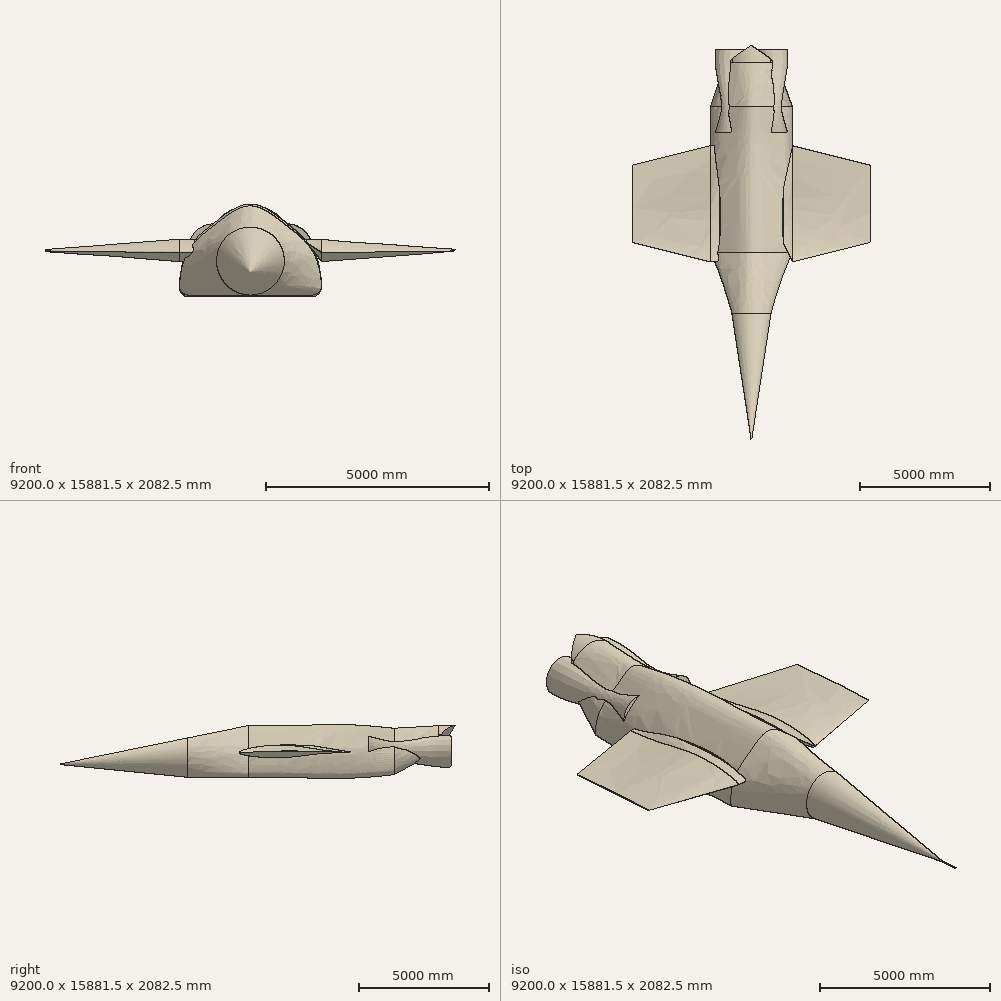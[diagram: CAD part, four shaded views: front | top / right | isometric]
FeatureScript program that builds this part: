
annotation { "Feature Type Name" : "Feature", "Feature Type Description" : "" }
export const myFeature = defineFeature(function(context is Context, id is Id, definition is map)
    precondition{}
    {
        {
            var Q0;
            Q0=qCreatedBy(makeId("Right.planeOp"),FACE);
            var sketch = newSketch(context, id + "F0", { "sketchPlane" : qUnion([Q0])});
            skLineSegment(sketch, "E0", {"start": v(0, 0) * mm, "end": v(-1750, 0) * mm});
            skLineSegment(sketch, "E1", {"start": v(-1750, 0) * mm, "end": v(-3500, 0) * mm});
            skLineSegment(sketch, "E2", {"start": v(-3500, 0) * mm, "end": v(-3500, -1000) * mm});
            skLineSegment(sketch, "E3", {"start": v(-3500, -1000) * mm, "end": v(-8500, -1000) * mm});
            skLineSegment(sketch, "E4", {"start": v(-8500, -1000) * mm, "end": v(-8500, -499.31) * mm});
            skLineSegment(sketch, "E5", {"start": v(-1151.4, 0) * mm, "end": v(-1151.4, 1000) * mm});
            skLineSegment(sketch, "E6", {"start": v(-1151.4, 1000) * mm, "end": v(-8500, -499.31) * mm});
            skLineSegment(sketch, "E7", {"start": v(-8500, -499.31) * mm, "end": v(-3500, -1000) * mm});
            skLineSegment(sketch, "E8", {"start": v(-3500, 0) * mm, "end": v(-3500, 520.82) * mm});
            skLineSegment(sketch, "E9", {"start": v(-8500, -499.31) * mm, "end": v(-8450, -499.31) * mm});
            skLineSegment(sketch, "E10", {"start": v(-8450, -499.31) * mm, "end": v(-8450, -489.1) * mm});
            skLineSegment(sketch, "E11", {"start": v(-8450, -499.31) * mm, "end": v(-8450, -504.32) * mm});
            skSolve(sketch);
        }
        {
            var Q0;
            Q0=sQuery(id+"F0.wireOp",EDGE,"E5");
            cPlane(context, id + "F1", {"entities" : qUnion([Q0]), "cplaneType" : CPlaneType.LINE_ANGLE, "offset" : 25 * mm, "angle" : 90 * degree, "oppositeDirection" : true, "width" : 150 * mm, "height" : 150 * mm});
        }
        {
            var Q0;
            Q0=qCreatedBy(id+"F1.planeOp",FACE);
            var sketch = newSketch(context, id + "F2", { "sketchPlane" : qUnion([Q0])});
            skLineSegment(sketch, "E12.top", {"start": v(-1394.2, -1000) * mm, "end": v(1394.2, -1000) * mm});
            skPoint(sketch, "E12.middle", {"position": v(0, 0) * mm});
            skFitSpline(sketch, "E13", {"points": [v(-1600, -1000) * mm, v(-848, 530) * mm, v(0, 1000) * mm, v(848, 530) * mm, v(1600, -1000) * mm], "startDerivative": vector(0, 10524.75) * mm, "endDerivative": vector(0, -10524.75) * mm});
            skArc(sketch, "E14", {"start": v(-735.27, 618.52) * mm, "mid": v(-1273.27, 435.52) * mm, "end": v(-1440.68, -107.53) * mm});
            skArc(sketch, "E15", {"start": v(1440.68, -107.53) * mm, "mid": v(1273.27, 435.52) * mm, "end": v(735.27, 618.52) * mm});
            skFitSpline(sketch, "E16.trimOffspring", {"points": [v(-1600, -1000) * mm, v(-848, 530) * mm, v(0, 1000) * mm, v(848, 530) * mm, v(1600, -1000) * mm], "startDerivative": vector(0, 10524.75) * mm, "endDerivative": vector(0, -10524.75) * mm});
            skFitSpline(sketch, "E17.trimOffspring", {"points": [v(-1600, -1000) * mm, v(-848, 530) * mm, v(0, 1000) * mm, v(848, 530) * mm, v(1600, -1000) * mm], "startDerivative": vector(0, 10524.75) * mm, "endDerivative": vector(0, -10524.75) * mm});
            skArc(sketch, "E18.filletArc", {"start": v(-1593.82, -787.83) * mm, "mid": v(-1539.85, -937.05) * mm, "end": v(-1394.2, -1000) * mm});
            skArc(sketch, "E19.filletArc", {"start": v(1394.2, -1000) * mm, "mid": v(1539.85, -937.05) * mm, "end": v(1593.82, -787.83) * mm});
            skSolve(sketch);
        }
        {
            var Q0;
            Q0=qCreatedBy(makeId("Front.planeOp"),FACE);
            var sketch = newSketch(context, id + "F3", { "sketchPlane" : qUnion([Q0])});
            skLineSegment(sketch, "E20.top", {"start": v(-1394.2, -1000) * mm, "end": v(1394.2, -1000) * mm});
            skPoint(sketch, "E20.middle", {"position": v(0, 0) * mm});
            skFitSpline(sketch, "E21", {"points": [v(-1600, -1000) * mm, v(-848, 530) * mm, v(0, 1000) * mm, v(848, 530) * mm, v(1600, -1000) * mm], "startDerivative": vector(0, 10524.75) * mm, "endDerivative": vector(0, -10524.75) * mm});
            skArc(sketch, "E22", {"start": v(-735.27, 618.52) * mm, "mid": v(-1273.27, 435.52) * mm, "end": v(-1440.68, -107.53) * mm});
            skArc(sketch, "E23", {"start": v(1440.68, -107.53) * mm, "mid": v(1273.27, 435.52) * mm, "end": v(735.27, 618.52) * mm});
            skFitSpline(sketch, "E24.trimOffspring", {"points": [v(-1600, -1000) * mm, v(-848, 530) * mm, v(0, 1000) * mm, v(848, 530) * mm, v(1600, -1000) * mm], "startDerivative": vector(0, 10524.75) * mm, "endDerivative": vector(0, -10524.75) * mm});
            skFitSpline(sketch, "E25.trimOffspring", {"points": [v(-1600, -1000) * mm, v(-848, 530) * mm, v(0, 1000) * mm, v(848, 530) * mm, v(1600, -1000) * mm], "startDerivative": vector(0, 10524.75) * mm, "endDerivative": vector(0, -10524.75) * mm});
            skArc(sketch, "E26.filletArc", {"start": v(-1593.82, -787.83) * mm, "mid": v(-1539.85, -937.05) * mm, "end": v(-1394.2, -1000) * mm});
            skArc(sketch, "E27.filletArc", {"start": v(1394.2, -1000) * mm, "mid": v(1539.85, -937.05) * mm, "end": v(1593.82, -787.83) * mm});
            skSolve(sketch);
        }
        {
            var Q0;
            Q0=qCreatedBy(makeId("Front.planeOp"),FACE);
            cPlane(context, id + "F4", {"entities" : qUnion([Q0]), "cplaneType" : CPlaneType.OFFSET, "offset" : 3500 * mm, "oppositeDirection" : true, "width" : 150 * mm, "height" : 150 * mm});
        }
        {
            var Q0;
            Q0=qCreatedBy(id+"F4.planeOp",FACE);
            var sketch = newSketch(context, id + "F5", { "sketchPlane" : qUnion([Q0])});
            skLineSegment(sketch, "E28.top", {"start": v(-1394.2, -1000) * mm, "end": v(1394.2, -1000) * mm});
            skPoint(sketch, "E28.middle", {"position": v(0, 0) * mm});
            skFitSpline(sketch, "E29", {"points": [v(-1600, -1000) * mm, v(-848, 530) * mm, v(0, 1000) * mm, v(848, 530) * mm, v(1600, -1000) * mm], "startDerivative": vector(0, 10524.75) * mm, "endDerivative": vector(0, -10524.75) * mm});
            skArc(sketch, "E30", {"start": v(-735.27, 618.52) * mm, "mid": v(-1273.27, 435.52) * mm, "end": v(-1440.68, -107.53) * mm});
            skArc(sketch, "E31", {"start": v(1440.68, -107.53) * mm, "mid": v(1273.27, 435.52) * mm, "end": v(735.27, 618.52) * mm});
            skFitSpline(sketch, "E32.trimOffspring", {"points": [v(-1600, -1000) * mm, v(-848, 530) * mm, v(0, 1000) * mm, v(848, 530) * mm, v(1600, -1000) * mm], "startDerivative": vector(0, 10524.75) * mm, "endDerivative": vector(0, -10524.75) * mm});
            skFitSpline(sketch, "E33.trimOffspring", {"points": [v(-1600, -1000) * mm, v(-848, 530) * mm, v(0, 1000) * mm, v(848, 530) * mm, v(1600, -1000) * mm], "startDerivative": vector(0, 10524.75) * mm, "endDerivative": vector(0, -10524.75) * mm});
            skArc(sketch, "E34.filletArc", {"start": v(-1593.82, -787.83) * mm, "mid": v(-1539.85, -937.05) * mm, "end": v(-1394.2, -1000) * mm});
            skArc(sketch, "E35.filletArc", {"start": v(1394.2, -1000) * mm, "mid": v(1539.85, -937.05) * mm, "end": v(1593.82, -787.83) * mm});
            skSolve(sketch);
        }
        {
            var Q0;
            Q0=qCreatedBy(makeId("Front.planeOp"),FACE);
            cPlane(context, id + "F6", {"entities" : qUnion([Q0]), "cplaneType" : CPlaneType.OFFSET, "offset" : 4500 * mm, "oppositeDirection" : true, "width" : 150 * mm, "height" : 150 * mm});
        }
        {
            var Q0;
            Q0=qCreatedBy(id+"F6.planeOp",FACE);
            var sketch = newSketch(context, id + "F7", { "sketchPlane" : qUnion([Q0])});
            skLineSegment(sketch, "E36.top", {"start": v(-1413.07, -900) * mm, "end": v(1413.07, -900) * mm});
            skPoint(sketch, "E36.middle", {"position": v(0, 0) * mm});
            skFitSpline(sketch, "E37", {"points": [v(-1600, -900) * mm, v(-784.42, 441.24) * mm, v(0, 900) * mm, v(784.42, 441.24) * mm, v(1600, -900) * mm], "startDerivative": vector(0, 9508.62) * mm, "endDerivative": vector(0, -9508.62) * mm});
            skArc(sketch, "E38", {"start": v(-719.25, 488.69) * mm, "mid": v(-1131.76, 394.84) * mm, "end": v(-1324.66, 18.33) * mm});
            skArc(sketch, "E39", {"start": v(1324.66, 18.33) * mm, "mid": v(1131.76, 394.84) * mm, "end": v(719.25, 488.69) * mm});
            skFitSpline(sketch, "E40.trimOffspring", {"points": [v(-1600, -900) * mm, v(-784.42, 441.24) * mm, v(0, 900) * mm, v(784.42, 441.24) * mm, v(1600, -900) * mm], "startDerivative": vector(0, 9508.62) * mm, "endDerivative": vector(0, -9508.62) * mm});
            skFitSpline(sketch, "E41.trimOffspring", {"points": [v(-1600, -900) * mm, v(-784.42, 441.24) * mm, v(0, 900) * mm, v(784.42, 441.24) * mm, v(1600, -900) * mm], "startDerivative": vector(0, 9508.62) * mm, "endDerivative": vector(0, -9508.62) * mm});
            skArc(sketch, "E42.filletArc", {"start": v(-1592.48, -705.43) * mm, "mid": v(-1545.4, -842.02) * mm, "end": v(-1413.07, -900) * mm});
            skArc(sketch, "E43.filletArc", {"start": v(1413.07, -900) * mm, "mid": v(1545.4, -842.02) * mm, "end": v(1592.48, -705.43) * mm});
            skLineSegment(sketch, "E44", {"start": v(-719.25, 488.69) * mm, "end": v(-1324.66, 18.33) * mm, "construction": true});
            skLineSegment(sketch, "E45", {"start": v(719.25, 488.69) * mm, "end": v(1324.66, 18.33) * mm, "construction": true});
            skSolve(sketch);
        }
        {
            var Q0;
            Q0=qCreatedBy(makeId("Front.planeOp"),FACE);
            cPlane(context, id + "F8", {"entities" : qUnion([Q0]), "cplaneType" : CPlaneType.OFFSET, "offset" : 6232.05 * mm, "oppositeDirection" : true, "width" : 150 * mm, "height" : 150 * mm});
        }
        {
            var Q0;
            Q0=qCreatedBy(id+"F8.planeOp",FACE);
            var sketch = newSketch(context, id + "F9", { "sketchPlane" : qUnion([Q0])});
            skArc(sketch, "E46", {"start": v(998.61, 52.63) * mm, "mid": v(0, 1000) * mm, "end": v(-998.61, 52.63) * mm});
            skLineSegment(sketch, "E47", {"start": v(0, 0) * mm, "end": v(-948.68, 0) * mm});
            skLineSegment(sketch, "E48", {"start": v(0, 0) * mm, "end": v(948.68, 0) * mm});
            skLineSegment(sketch, "E49", {"start": v(0, 1000) * mm, "end": v(0, 675) * mm, "construction": true});
            skLineSegment(sketch, "E50", {"start": v(0, 675) * mm, "end": v(-737.82, 675) * mm, "construction": true});
            skLineSegment(sketch, "E51", {"start": v(0, 675) * mm, "end": v(737.82, 675) * mm, "construction": true});
            skPoint(sketch, "E52.visualSharp", {"position": v(-1000, 0) * mm});
            skArc(sketch, "E52.filletArc", {"start": v(-998.61, 52.63) * mm, "mid": v(-984.96, 15.59) * mm, "end": v(-948.68, 0) * mm});
            skPoint(sketch, "E53.visualSharp", {"position": v(1000, 0) * mm});
            skArc(sketch, "E53.filletArc", {"start": v(948.68, 0) * mm, "mid": v(984.96, 15.59) * mm, "end": v(998.61, 52.63) * mm});
            skSolve(sketch);
        }
        {
            var Q0;
            Q0=makeQuery(id+"F2.imprint","IMPRINT",FACE,{"disambiguationData":[TD([[makeQuery(id+"F2.imprint","IMPRINT",EDGE,{"derivedFrom":sQuery(id+"F2.wireOp",EDGE,"E12.top")}),1.0]])]});
            var Q1;
            Q1=makeQuery(id+"F3.imprint","IMPRINT",FACE,{"disambiguationData":[TD([[makeQuery(id+"F3.imprint","IMPRINT",EDGE,{"derivedFrom":sQuery(id+"F3.wireOp",EDGE,"E20.top")}),1.0]])]});
            var Q2;
            Q2=makeQuery(id+"F5.imprint","IMPRINT",FACE,{"disambiguationData":[TD([[makeQuery(id+"F5.imprint","IMPRINT",EDGE,{"derivedFrom":sQuery(id+"F5.wireOp",EDGE,"E28.top")}),1.0]])]});
            var Q3;
            Q3=makeQuery(id+"F7.imprint","IMPRINT",FACE,{"disambiguationData":[TD([[makeQuery(id+"F7.imprint","IMPRINT",EDGE,{"derivedFrom":sQuery(id+"F7.wireOp",EDGE,"E36.top")}),1.0]])]});
            loft(context, id + "F10", {"sheetProfilesArray" : [{ "sheetProfileEntities" : qUnion([Q0]) }, { "sheetProfileEntities" : qUnion([Q1]) }, { "sheetProfileEntities" : qUnion([Q2]) }, { "sheetProfileEntities" : qUnion([Q3]) }]});
        }
        {
            var Q0;
            Q0=sQuery(id+"F7.wireOp",EDGE,"E44");
            var Q1;
            Q1=sQuery(id+"F9.wireOp",VERTEX,"E50.end");
            cPlane(context, id + "F11", {"entities" : qUnion([Q0, Q1]), "cplaneType" : CPlaneType.LINE_ANGLE, "offset" : 25 * mm, "angle" : 180 * degree, "width" : 150 * mm, "height" : 150 * mm});
        }
        {
            var Q0;
            Q0=qCreatedBy(id+"F11.planeOp",FACE);
            var sketch = newSketch(context, id + "F12", { "sketchPlane" : qUnion([Q0])});
            skLineSegment(sketch, "E54", {"start": v(-589.34, 4526.34) * mm, "end": v(-612.8, 6268.32) * mm});
            skLineSegment(sketch, "E55", {"start": v(-1354.08, 4472.19) * mm, "end": v(-612.8, 6268.32) * mm});
            skSolve(sketch);
        }
        {
            var Q0;
            Q0=sQuery(id+"F7.wireOp",EDGE,"E45");
            var Q1;
            Q1=sQuery(id+"F9.wireOp",VERTEX,"E51.end");
            cPlane(context, id + "F13", {"entities" : qUnion([Q0, Q1]), "cplaneType" : CPlaneType.LINE_ANGLE, "offset" : 25 * mm, "angle" : 0 * degree, "width" : 150 * mm, "height" : 150 * mm});
        }
        {
            var Q0;
            Q0=qCreatedBy(id+"F13.planeOp",FACE);
            var sketch = newSketch(context, id + "F14", { "sketchPlane" : qUnion([Q0])});
            skLineSegment(sketch, "E56", {"start": v(589.34, 4526.34) * mm, "end": v(612.8, 6268.32) * mm});
            skLineSegment(sketch, "E57", {"start": v(1354.08, 4472.19) * mm, "end": v(612.8, 6268.32) * mm});
            skSolve(sketch);
        }
        {
            var Q1;
            Q1=makeQuery(id+"F10.opLoft","CAP_FACE",FACE,{"disambiguationData":[OSD([makeQuery(id+"F7.imprint","IMPRINT",FACE,{"disambiguationData":[TD([[makeQuery(id+"F7.imprint","IMPRINT",EDGE,{"derivedFrom":sQuery(id+"F7.wireOp",EDGE,"E36.top")}),1.0]])]})])],"isStart":true});
            var Q2;
            Q2=makeQuery(id+"F9.imprint","IMPRINT",FACE,{"disambiguationData":[TD([[makeQuery(id+"F9.imprint","IMPRINT",EDGE,{"derivedFrom":sQuery(id+"F9.wireOp",EDGE,"E46")}),1.0]])]});
            var Q3;
            Q3=sQuery(id+"F12.wireOp",EDGE,"E54");
            var Q4;
            Q4=sQuery(id+"F14.wireOp",EDGE,"E56");
            loft(context, id + "F15", {"operationType" : NewBodyOperationType.ADD, "addGuides" : true, "sheetProfilesArray" : [{ "sheetProfileEntities" : qUnion([Q1]) }, { "sheetProfileEntities" : qUnion([Q2]) }], "guidesArray" : [{ "guideEntities" : qUnion([Q3]), "guideDerivativeType" : LoftGuideDerivativeType.DEFAULT, "guideDerivativeMagnitude" : 1 }, { "guideEntities" : qUnion([Q4]), "guideDerivativeType" : LoftGuideDerivativeType.DEFAULT, "guideDerivativeMagnitude" : 1 }]});
        }
        {
            var Q0;
            Q0=makeQuery(id+"F15.opLoft","CAP_FACE",FACE,{"disambiguationData":[OSD([makeQuery(id+"F9.imprint","IMPRINT",FACE,{"disambiguationData":[TD([[makeQuery(id+"F9.imprint","IMPRINT",EDGE,{"derivedFrom":sQuery(id+"F9.wireOp",EDGE,"E46")}),1.0]])]})])],"isStart":true});
            extrude(context, id + "F16", {"entities" : qUnion([Q0]), "operationType" : NewBodyOperationType.ADD, "depth" : 649.4 * mm, "offsetDistance" : 25 * mm});
        }
        {
            var Q0;
            Q0=qCreatedBy(makeId("Right.planeOp"),FACE);
            var sketch = newSketch(context, id + "F17", { "sketchPlane" : qUnion([Q0])});
            skLineSegment(sketch, "E58", {"start": v(0, 0) * mm, "end": v(4500, 0) * mm});
            skLineSegment(sketch, "E59", {"start": v(4500, 0) * mm, "end": v(6232.05, 0) * mm});
            skLineSegment(sketch, "E60", {"start": v(4500, 0) * mm, "end": v(4500, 1000) * mm});
            skLineSegment(sketch, "E61", {"start": v(4500, 1000) * mm, "end": v(6881.46, 1000) * mm});
            skLineSegment(sketch, "E62", {"start": v(6881.46, 1000) * mm, "end": v(6881.46, -1000) * mm});
            skLineSegment(sketch, "E63", {"start": v(6881.46, 1000) * mm, "end": v(6232.05, 0) * mm});
            skLineSegment(sketch, "E64", {"start": v(6232.05, 0) * mm, "end": v(5582.64, -1000) * mm});
            skLineSegment(sketch, "E65", {"start": v(5582.64, -1000) * mm, "end": v(6881.46, -1000) * mm});
            skSolve(sketch);
        }
        {
            var Q0;
            Q0=makeQuery(id+"F17.imprint","IMPRINT",FACE,{"disambiguationData":[TD([[makeQuery(id+"F17.imprint","IMPRINT",EDGE,{"derivedFrom":sQuery(id+"F17.wireOp",EDGE,"E62")}),-1.0]])]});
            var Q1;
            Q1=sQuery(id+"F17.wireOp",EDGE,"E61");
            revolve(context, id + "F18", {"operationType" : NewBodyOperationType.REMOVE, "entities" : qUnion([Q0]), "axis" : qUnion([Q1]), "revolveType" : RevolveType.SYMMETRIC, "oppositeDirection" : true, "angle" : 182 * degree});
        }
        {
            var Q0;
            Q0=qCreatedBy(id+"F1.planeOp",FACE);
            var sketch = newSketch(context, id + "F19", { "sketchPlane" : qUnion([Q0])});
            skLineSegment(sketch, "E66.top", {"start": v(-1394.2, -1000) * mm, "end": v(1394.2, -1000) * mm});
            skPoint(sketch, "E66.middle", {"position": v(0, 0) * mm});
            skFitSpline(sketch, "E67", {"points": [v(-1600, -1000) * mm, v(-848, 530) * mm, v(0, 1000) * mm, v(848, 530) * mm, v(1600, -1000) * mm], "startDerivative": vector(0, 10524.75) * mm, "endDerivative": vector(0, -10524.75) * mm});
            skArc(sketch, "E68.filletArc", {"start": v(-1593.82, -787.83) * mm, "mid": v(-1539.85, -937.05) * mm, "end": v(-1394.2, -1000) * mm});
            skArc(sketch, "E69.filletArc", {"start": v(1394.2, -1000) * mm, "mid": v(1539.85, -937.05) * mm, "end": v(1593.82, -787.83) * mm});
            skLineSegment(sketch, "E70", {"start": v(-1593.82, -787.83) * mm, "end": v(-1394.2, -1000) * mm, "construction": true});
            skLineSegment(sketch, "E71", {"start": v(1593.82, -787.83) * mm, "end": v(1394.2, -1000) * mm, "construction": true});
            skSolve(sketch);
        }
        {
            var Q0;
            Q0=qCreatedBy(makeId("Front.planeOp"),FACE);
            cPlane(context, id + "F20", {"entities" : qUnion([Q0]), "cplaneType" : CPlaneType.OFFSET, "offset" : 3500 * mm, "width" : 150 * mm, "height" : 150 * mm});
        }
        {
            var Q0;
            Q0=qCreatedBy(id+"F20.planeOp",FACE);
            var sketch = newSketch(context, id + "F21", { "sketchPlane" : qUnion([Q0])});
            skCircle(sketch, "E72", {"center": v(0, -239.59) * mm, "radius": 760.41 * mm});
            skLineSegment(sketch, "E73", {"start": v(0, -1000) * mm, "end": v(0, -800) * mm, "construction": true});
            skLineSegment(sketch, "E74", {"start": v(0, -800) * mm, "end": v(-513.97, -800) * mm, "construction": true});
            skLineSegment(sketch, "E75", {"start": v(0, -800) * mm, "end": v(513.97, -800) * mm, "construction": true});
            skSolve(sketch);
        }
        {
            var Q0;
            Q0=qCreatedBy(makeId("Front.planeOp"),FACE);
            cPlane(context, id + "F22", {"entities" : qUnion([Q0]), "cplaneType" : CPlaneType.OFFSET, "offset" : 8450 * mm, "width" : 150 * mm, "height" : 150 * mm});
        }
        {
            var Q0;
            Q0=qCreatedBy(id+"F22.planeOp",FACE);
            var sketch = newSketch(context, id + "F23", { "sketchPlane" : qUnion([Q0])});
            skCircle(sketch, "E76", {"center": v(0, -496.71) * mm, "radius": 7.6 * mm});
            skSolve(sketch);
        }
        {
            var Q0;
            Q0=sQuery(id+"F19.wireOp",EDGE,"E70");
            var Q1;
            Q1=sQuery(id+"F21.wireOp",VERTEX,"E74.end");
            cPlane(context, id + "F24", {"entities" : qUnion([Q0, Q1]), "cplaneType" : CPlaneType.LINE_ANGLE, "offset" : 25 * mm, "angle" : 0 * degree, "width" : 150 * mm, "height" : 150 * mm});
        }
        {
            var Q0;
            Q0=qCreatedBy(id+"F24.planeOp",FACE);
            var sketch = newSketch(context, id + "F25", { "sketchPlane" : qUnion([Q0])});
            skLineSegment(sketch, "E77", {"start": v(3032.27, -230.44) * mm, "end": v(558.11, 518.4) * mm});
            skLineSegment(sketch, "E78", {"start": v(3032.27, -230.44) * mm, "end": v(558.11, 227.09) * mm});
            skSolve(sketch);
        }
        {
            var Q0;
            Q0=sQuery(id+"F19.wireOp",EDGE,"E71");
            var Q1;
            Q1=sQuery(id+"F21.wireOp",VERTEX,"E75.end");
            cPlane(context, id + "F26", {"entities" : qUnion([Q0, Q1]), "cplaneType" : CPlaneType.LINE_ANGLE, "offset" : 25 * mm, "angle" : 180 * degree, "width" : 150 * mm, "height" : 150 * mm});
        }
        {
            var Q0;
            Q0=qCreatedBy(id+"F26.planeOp",FACE);
            var sketch = newSketch(context, id + "F27", { "sketchPlane" : qUnion([Q0])});
            skLineSegment(sketch, "E79", {"start": v(-3032.27, -230.44) * mm, "end": v(-558.11, 518.4) * mm});
            skLineSegment(sketch, "E80", {"start": v(-3032.27, -230.44) * mm, "end": v(-558.11, 227.09) * mm});
            skSolve(sketch);
        }
        {
            var Q1;
            Q1=makeQuery(id+"F19.imprint","IMPRINT",FACE,{"disambiguationData":[TD([[makeQuery(id+"F19.imprint","IMPRINT",EDGE,{"derivedFrom":sQuery(id+"F19.wireOp",EDGE,"E66.top")}),1.0]])]});
            var Q2;
            Q2=makeQuery(id+"F21.imprint","IMPRINT",FACE,{"disambiguationData":[TD([[makeQuery(id+"F21.imprint","IMPRINT",EDGE,{"derivedFrom":sQuery(id+"F21.wireOp",EDGE,"E72")}),1.0]])]});
            var Q3;
            Q3=sQuery(id+"F25.wireOp",EDGE,"E77");
            var Q4;
            Q4=sQuery(id+"F27.wireOp",EDGE,"E79");
            loft(context, id + "F28", {"operationType" : NewBodyOperationType.ADD, "addGuides" : true, "sheetProfilesArray" : [{ "sheetProfileEntities" : qUnion([Q1]) }, { "sheetProfileEntities" : qUnion([Q2]) }], "guidesArray" : [{ "guideEntities" : qUnion([Q3]), "guideDerivativeType" : LoftGuideDerivativeType.DEFAULT, "guideDerivativeMagnitude" : 1 }, { "guideEntities" : qUnion([Q4]), "guideDerivativeType" : LoftGuideDerivativeType.DEFAULT, "guideDerivativeMagnitude" : 1 }]});
        }
        {
            var Q1;
            Q1=makeQuery(id+"F28.opLoft","CAP_FACE",FACE,{"disambiguationData":[OSD([makeQuery(id+"F21.imprint","IMPRINT",FACE,{"disambiguationData":[TD([[makeQuery(id+"F21.imprint","IMPRINT",EDGE,{"derivedFrom":sQuery(id+"F21.wireOp",EDGE,"E72")}),1.0]])]})])],"isStart":true});
            var Q2;
            Q2=makeQuery(id+"F23.imprint","IMPRINT",FACE,{"disambiguationData":[TD([[makeQuery(id+"F23.imprint","IMPRINT",EDGE,{"derivedFrom":sQuery(id+"F23.wireOp",EDGE,"E76")}),1.0]])]});
            loft(context, id + "F29", {"operationType" : NewBodyOperationType.ADD, "sheetProfilesArray" : [{ "sheetProfileEntities" : qUnion([Q1]) }, { "sheetProfileEntities" : qUnion([Q2]) }]});
        }
        {
            var Q0;
            Q0=makeQuery(id+"F29.opLoft","CAP_FACE",FACE,{"disambiguationData":[OSD([makeQuery(id+"F23.imprint","IMPRINT",FACE,{"disambiguationData":[TD([[makeQuery(id+"F23.imprint","IMPRINT",EDGE,{"derivedFrom":sQuery(id+"F23.wireOp",EDGE,"E76")}),1.0]])]})])],"isStart":true});
            extrude(context, id + "F30", {"entities" : qUnion([Q0]), "operationType" : NewBodyOperationType.ADD, "depth" : 550 * mm, "offsetDistance" : 25 * mm});
        }
        {
            var Q0;
            Q0=qCreatedBy(makeId("Front.planeOp"),FACE);
            cPlane(context, id + "F31", {"entities" : qUnion([Q0]), "cplaneType" : CPlaneType.OFFSET, "offset" : 3500 * mm, "oppositeDirection" : true, "width" : 150 * mm, "height" : 150 * mm});
        }
        {
            var Q0;
            Q0=qCreatedBy(id+"F31.planeOp",FACE);
            var sketch = newSketch(context, id + "F32", { "sketchPlane" : qUnion([Q0])});
            skCircle(sketch, "E81", {"center": v(-800, 0) * mm, "radius": 600 * mm});
            skCircle(sketch, "E82", {"center": v(800, 0) * mm, "radius": 600 * mm});
            skSolve(sketch);
        }
        {
            var Q0;
            Q0=qCreatedBy(makeId("Front.planeOp"),FACE);
            cPlane(context, id + "F33", {"entities" : qUnion([Q0]), "cplaneType" : CPlaneType.OFFSET, "offset" : 4500 * mm, "oppositeDirection" : true, "width" : 150 * mm, "height" : 150 * mm});
        }
        {
            var Q0;
            Q0=qCreatedBy(id+"F33.planeOp",FACE);
            var sketch = newSketch(context, id + "F34", { "sketchPlane" : qUnion([Q0])});
            skCircle(sketch, "E83", {"center": v(-800, 0) * mm, "radius": 400 * mm});
            skCircle(sketch, "E84", {"center": v(800, 0) * mm, "radius": 400 * mm});
            skSolve(sketch);
        }
        {
            var Q0;
            Q0=qCreatedBy(makeId("Front.planeOp"),FACE);
            cPlane(context, id + "F35", {"entities" : qUnion([Q0]), "cplaneType" : CPlaneType.OFFSET, "offset" : 6232.05 * mm, "oppositeDirection" : true, "width" : 150 * mm, "height" : 150 * mm});
        }
        {
            var Q0;
            Q0=qCreatedBy(id+"F35.planeOp",FACE);
            var sketch = newSketch(context, id + "F36", { "sketchPlane" : qUnion([Q0])});
            skCircle(sketch, "E85", {"center": v(-800, 0) * mm, "radius": 600 * mm});
            skCircle(sketch, "E86", {"center": v(800, 0) * mm, "radius": 600 * mm});
            skSolve(sketch);
        }
        {
            var Q0;
            Q0=qCreatedBy(makeId("Front.planeOp"),FACE);
            cPlane(context, id + "F37", {"entities" : qUnion([Q0]), "cplaneType" : CPlaneType.OFFSET, "offset" : 6732.05 * mm, "oppositeDirection" : true, "width" : 150 * mm, "height" : 150 * mm});
        }
        {
            var Q0;
            Q0=qCreatedBy(id+"F37.planeOp",FACE);
            var sketch = newSketch(context, id + "F38", { "sketchPlane" : qUnion([Q0])});
            skCircle(sketch, "E87", {"center": v(-800, 0) * mm, "radius": 600 * mm});
            skCircle(sketch, "E88", {"center": v(800, 0) * mm, "radius": 600 * mm});
            skSolve(sketch);
        }
        {
            var Q0;
            Q0=makeQuery(id+"F32.imprint","IMPRINT",FACE,{"disambiguationData":[TD([[makeQuery(id+"F32.imprint","IMPRINT",EDGE,{"derivedFrom":sQuery(id+"F32.wireOp",EDGE,"E81")}),1.0]])]});
            var Q1;
            Q1=makeQuery(id+"F34.imprint","IMPRINT",FACE,{"disambiguationData":[TD([[makeQuery(id+"F34.imprint","IMPRINT",EDGE,{"derivedFrom":sQuery(id+"F34.wireOp",EDGE,"E83")}),1.0]])]});
            var Q2;
            Q2=makeQuery(id+"F36.imprint","IMPRINT",FACE,{"disambiguationData":[TD([[makeQuery(id+"F36.imprint","IMPRINT",EDGE,{"derivedFrom":sQuery(id+"F36.wireOp",EDGE,"E85")}),1.0]])]});
            var Q3;
            Q3=makeQuery(id+"F38.imprint","IMPRINT",FACE,{"disambiguationData":[TD([[makeQuery(id+"F38.imprint","IMPRINT",EDGE,{"derivedFrom":sQuery(id+"F38.wireOp",EDGE,"E87")}),1.0]])]});
            loft(context, id + "F39", {"sheetProfilesArray" : [{ "sheetProfileEntities" : qUnion([Q0]) }, { "sheetProfileEntities" : qUnion([Q1]) }, { "sheetProfileEntities" : qUnion([Q2]) }, { "sheetProfileEntities" : qUnion([Q3]) }]});
        }
        {
            var Q0;
            Q0=makeQuery(id+"F32.imprint","IMPRINT",FACE,{"disambiguationData":[TD([[makeQuery(id+"F32.imprint","IMPRINT",EDGE,{"derivedFrom":sQuery(id+"F32.wireOp",EDGE,"E82")}),1.0]])]});
            var Q1;
            Q1=makeQuery(id+"F34.imprint","IMPRINT",FACE,{"disambiguationData":[TD([[makeQuery(id+"F34.imprint","IMPRINT",EDGE,{"derivedFrom":sQuery(id+"F34.wireOp",EDGE,"E84")}),1.0]])]});
            var Q2;
            Q2=makeQuery(id+"F36.imprint","IMPRINT",FACE,{"disambiguationData":[TD([[makeQuery(id+"F36.imprint","IMPRINT",EDGE,{"derivedFrom":sQuery(id+"F36.wireOp",EDGE,"E86")}),1.0]])]});
            var Q3;
            Q3=makeQuery(id+"F38.imprint","IMPRINT",FACE,{"disambiguationData":[TD([[makeQuery(id+"F38.imprint","IMPRINT",EDGE,{"derivedFrom":sQuery(id+"F38.wireOp",EDGE,"E88")}),1.0]])]});
            loft(context, id + "F40", {"sheetProfilesArray" : [{ "sheetProfileEntities" : qUnion([Q0]) }, { "sheetProfileEntities" : qUnion([Q1]) }, { "sheetProfileEntities" : qUnion([Q2]) }, { "sheetProfileEntities" : qUnion([Q3]) }]});
        }
        {
            var Q0;
            Q0=qCreatedBy(makeId("Right.planeOp"),FACE);
            var sketch = newSketch(context, id + "F41", { "sketchPlane" : qUnion([Q0])});
            skFitSpline(sketch, "E89", {"points": [v(-1500, -50) * mm, v(0, 250) * mm, v(3000, -50) * mm, v(0, -250) * mm, v(-1500, -50) * mm]});
            skSolve(sketch);
        }
        {
            var Q0;
            Q0=qCreatedBy(makeId("Right.planeOp"),FACE);
            cPlane(context, id + "F42", {"entities" : qUnion([Q0]), "cplaneType" : CPlaneType.OFFSET, "offset" : 1600 * mm, "oppositeDirection" : true, "width" : 150 * mm, "height" : 150 * mm});
        }
        {
            var Q0;
            Q0=qCreatedBy(id+"F42.planeOp",FACE);
            var sketch = newSketch(context, id + "F43", { "sketchPlane" : qUnion([Q0])});
            skFitSpline(sketch, "E90", {"points": [v(-1500, -50) * mm, v(0, 250) * mm, v(3000, -50) * mm], "startDerivative": vector(0, 887.04) * mm, "endDerivative": vector(7705.35, -256.85) * mm});
            skFitSpline(sketch, "E91", {"points": [v(-1500, -50) * mm, v(0, -250) * mm, v(3000, -50) * mm], "startDerivative": vector(0, -722.87) * mm, "endDerivative": vector(7692.49, -256.42) * mm});
            skSolve(sketch);
        }
        {
            var Q0;
            Q0=qCreatedBy(makeId("Right.planeOp"),FACE);
            cPlane(context, id + "F44", {"entities" : qUnion([Q0]), "cplaneType" : CPlaneType.OFFSET, "offset" : 1600 * mm, "width" : 150 * mm, "height" : 150 * mm});
        }
        {
            var Q0;
            Q0=qCreatedBy(id+"F44.planeOp",FACE);
            var sketch = newSketch(context, id + "F45", { "sketchPlane" : qUnion([Q0])});
            skFitSpline(sketch, "E92", {"points": [v(-1500, -50) * mm, v(0, 250) * mm, v(3000, -50) * mm], "startDerivative": vector(0, 887.04) * mm, "endDerivative": vector(7705.35, -256.85) * mm});
            skFitSpline(sketch, "E93", {"points": [v(-1500, -50) * mm, v(0, -250) * mm, v(3000, -50) * mm], "startDerivative": vector(0, -722.87) * mm, "endDerivative": vector(7692.49, -256.42) * mm});
            skSolve(sketch);
        }
        {
            var Q0;
            Q0=qCreatedBy(makeId("Right.planeOp"),FACE);
            cPlane(context, id + "F46", {"entities" : qUnion([Q0]), "cplaneType" : CPlaneType.OFFSET, "offset" : 4600 * mm, "oppositeDirection" : true, "width" : 150 * mm, "height" : 150 * mm});
        }
        {
            var Q0;
            Q0=qCreatedBy(id+"F46.planeOp",FACE);
            var sketch = newSketch(context, id + "F47", { "sketchPlane" : qUnion([Q0])});
            skFitSpline(sketch, "E94", {"points": [v(-750, -10) * mm, v(250, 25) * mm, v(2250, -10) * mm], "startDerivative": vector(0, 162.94) * mm, "endDerivative": vector(5121.8, -51.22) * mm});
            skFitSpline(sketch, "E95", {"points": [v(-750, -10) * mm, v(750, -25) * mm, v(2250, -10) * mm], "startDerivative": vector(0, -60) * mm, "endDerivative": vector(6000, 0) * mm});
            skSolve(sketch);
        }
        {
            var Q0;
            Q0=qCreatedBy(makeId("Right.planeOp"),FACE);
            cPlane(context, id + "F48", {"entities" : qUnion([Q0]), "cplaneType" : CPlaneType.OFFSET, "offset" : 4600 * mm, "width" : 150 * mm, "height" : 150 * mm});
        }
        {
            var Q0;
            Q0=qCreatedBy(id+"F48.planeOp",FACE);
            var sketch = newSketch(context, id + "F49", { "sketchPlane" : qUnion([Q0])});
            skFitSpline(sketch, "E96", {"points": [v(-750, -10) * mm, v(0, 25) * mm, v(2250, -10) * mm], "startDerivative": vector(1773.58, 123.2) * mm, "endDerivative": vector(4025.46, -103.01) * mm});
            skFitSpline(sketch, "E97", {"points": [v(-750, -10) * mm, v(250, -25) * mm, v(2250, -10) * mm], "startDerivative": vector(2207.02, -49.02) * mm, "endDerivative": vector(3707.2, 43.71) * mm});
            skSolve(sketch);
        }
        {
            var Q0;
            Q0=qSketchRegion(id+"F41",true);
            extrude(context, id + "F50", {"entities" : qUnion([Q0]), "endBound" : BoundingType.SYMMETRIC, "depth" : 2500 * mm, "offsetDistance" : 25 * mm});
        }
        {
            var Q1;
            Q1=makeQuery(id+"F50.opExtrude","CAP_FACE",FACE,{"disambiguationData":[OSD([sQuery(id+"F41.wireOp",EDGE,"E89")])],"isStart":true});
            var Q2;
            {var subQ0=sQuery(id+"F43.wireOp",EDGE,"E90");Q2=makeQuery(id+"F43.imprint","IMPRINT",FACE,{"disambiguationData":[TD([[makeQuery(id+"F43.imprint","IMPRINT",EDGE,{"derivedFrom":subQ0}),-1.0]])]});}
            loft(context, id + "F51", {"operationType" : NewBodyOperationType.ADD, "sheetProfilesArray" : [{ "sheetProfileEntities" : qUnion([Q1]) }, { "sheetProfileEntities" : qUnion([Q2]) }]});
        }
        {
            var Q1;
            Q1=makeQuery(id+"F50.opExtrude","CAP_FACE",FACE,{"disambiguationData":[OSD([sQuery(id+"F41.wireOp",EDGE,"E89")])],"isStart":false});
            var Q2;
            {var subQ0=sQuery(id+"F45.wireOp",EDGE,"E92");Q2=makeQuery(id+"F45.imprint","IMPRINT",FACE,{"disambiguationData":[TD([[makeQuery(id+"F45.imprint","IMPRINT",EDGE,{"derivedFrom":subQ0}),-1.0]])]});}
            loft(context, id + "F52", {"operationType" : NewBodyOperationType.ADD, "sheetProfilesArray" : [{ "sheetProfileEntities" : qUnion([Q1]) }, { "sheetProfileEntities" : qUnion([Q2]) }]});
        }
        {
            var Q1;
            {var subQ0=sQuery(id+"F43.wireOp",EDGE,"E90");Q1=makeQuery(id+"F51.opLoft","CAP_FACE",FACE,{"disambiguationData":[OSD([makeQuery(id+"F43.imprint","IMPRINT",FACE,{"disambiguationData":[TD([[makeQuery(id+"F43.imprint","IMPRINT",EDGE,{"derivedFrom":subQ0}),-1.0]])]})])],"isStart":true});}
            var Q2;
            Q2=makeQuery(id+"F47.imprint","IMPRINT",FACE,{"disambiguationData":[TD([[makeQuery(id+"F47.imprint","IMPRINT",EDGE,{"derivedFrom":sQuery(id+"F47.wireOp",EDGE,"E94")}),-1.0]])]});
            loft(context, id + "F53", {"operationType" : NewBodyOperationType.ADD, "sheetProfilesArray" : [{ "sheetProfileEntities" : qUnion([Q1]) }, { "sheetProfileEntities" : qUnion([Q2]) }]});
        }
        {
            var Q1;
            {var subQ0=sQuery(id+"F45.wireOp",EDGE,"E92");Q1=makeQuery(id+"F52.opLoft","CAP_FACE",FACE,{"disambiguationData":[OSD([makeQuery(id+"F45.imprint","IMPRINT",FACE,{"disambiguationData":[TD([[makeQuery(id+"F45.imprint","IMPRINT",EDGE,{"derivedFrom":subQ0}),-1.0]])]})])],"isStart":true});}
            var Q2;
            Q2=makeQuery(id+"F49.imprint","IMPRINT",FACE,{"disambiguationData":[TD([[makeQuery(id+"F49.imprint","IMPRINT",EDGE,{"derivedFrom":sQuery(id+"F49.wireOp",EDGE,"E96")}),-1.0]])]});
            loft(context, id + "F54", {"operationType" : NewBodyOperationType.ADD, "sheetProfilesArray" : [{ "sheetProfileEntities" : qUnion([Q1]) }, { "sheetProfileEntities" : qUnion([Q2]) }]});
        }
    });
